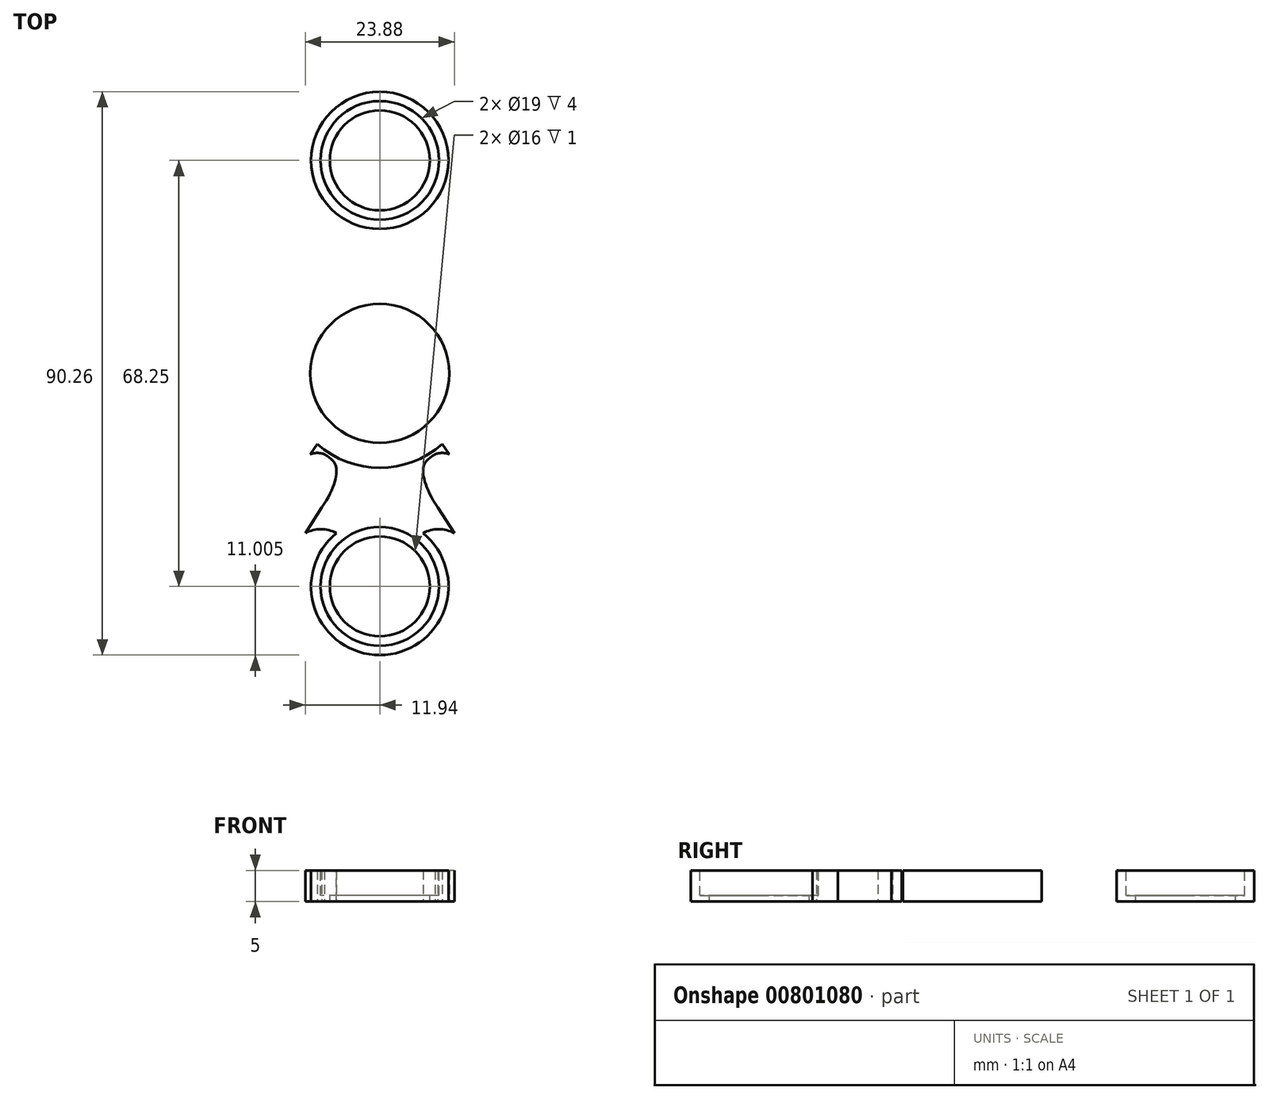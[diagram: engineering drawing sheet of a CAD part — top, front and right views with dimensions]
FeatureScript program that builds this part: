
annotation { "Feature Type Name" : "Feature", "Feature Type Description" : "" }
export const myFeature = defineFeature(function(context is Context, id is Id, definition is map)
    precondition{}
    {
        {
            var Q0;
            Q0=qCreatedBy(makeId("Top.planeOp"),FACE);
            var sketch = newSketch(context, id + "F0", { "sketchPlane" : qUnion([Q0])});
            skCircle(sketch, "E0", {"center": v(0, 0) * mm, "radius": 11.12 * mm});
            skCircle(sketch, "E1", {"center": v(0, 0) * mm, "radius": 15.12 * mm});
            skLineSegment(sketch, "E2", {"start": v(0, 15.12) * mm, "end": v(0, 45.12) * mm});
            skLineSegment(sketch, "E3", {"start": v(0, 45.12) * mm, "end": v(0, 23.12) * mm});
            skCircle(sketch, "E4", {"center": v(0, 34.12) * mm, "radius": 11 * mm});
            skLineSegment(sketch, "E5", {"start": v(0, 34.12) * mm, "end": v(-11, 34.12) * mm});
            skLineSegment(sketch, "E6", {"start": v(-10, 11.35) * mm, "end": v(-11.17, 12.98) * mm});
            skArc(sketch, "E7", {"start": v(-11.17, 12.98) * mm, "mid": v(-10, 12.75) * mm, "end": v(-8.84, 12.98) * mm});
            skArc(sketch, "E8", {"start": v(-11.94, 25.6) * mm, "mid": v(-9.45, 24.97) * mm, "end": v(-6.96, 25.6) * mm});
            skLineSegment(sketch, "E9", {"start": v(-11.94, 25.6) * mm, "end": v(-9.3, 21.5) * mm});
            skFitSpline(sketch, "E10", {"points": [v(-9.3, 21.5) * mm, v(-6.96, 15.22) * mm, v(-8.84, 12.98) * mm], "startDerivative": vector(9.24, -13.6) * mm, "endDerivative": vector(-10.35, -6.73) * mm});
            skLineSegment(sketch, "E11.MirrorCS", {"start": v(10, 11.35) * mm, "end": v(11.17, 12.98) * mm});
            skArc(sketch, "E12.MirrorCS", {"start": v(11.17, 12.98) * mm, "mid": v(10, 12.75) * mm, "end": v(8.84, 12.98) * mm});
            skFitSpline(sketch, "E13.MirrorCS", {"points": [v(9.3, 21.5) * mm, v(6.96, 15.22) * mm, v(8.84, 12.98) * mm], "startDerivative": vector(-9.24, -13.6) * mm, "endDerivative": vector(10.35, -6.73) * mm});
            skLineSegment(sketch, "E14.MirrorCS", {"start": v(11.94, 25.6) * mm, "end": v(9.3, 21.5) * mm});
            skArc(sketch, "E15.MirrorCS", {"start": v(11.94, 25.6) * mm, "mid": v(9.45, 24.97) * mm, "end": v(6.96, 25.6) * mm});
            skArc(sketch, "E16.MirrorCS", {"start": v(11.17, -12.98) * mm, "mid": v(10, -12.75) * mm, "end": v(8.84, -12.98) * mm});
            skLineSegment(sketch, "E17.MirrorCS", {"start": v(10, -11.35) * mm, "end": v(11.17, -12.98) * mm});
            skArc(sketch, "E18.MirrorCS", {"start": v(-11.17, -12.98) * mm, "mid": v(-10, -12.75) * mm, "end": v(-8.84, -12.98) * mm});
            skLineSegment(sketch, "E19.MirrorCS", {"start": v(-10, -11.35) * mm, "end": v(-11.17, -12.98) * mm});
            skArc(sketch, "E20.MirrorCS", {"start": v(11.94, -25.6) * mm, "mid": v(9.45, -24.97) * mm, "end": v(6.96, -25.6) * mm});
            skFitSpline(sketch, "E21.MirrorCS", {"points": [v(-9.3, -21.5) * mm, v(-6.96, -15.22) * mm, v(-8.84, -12.98) * mm], "startDerivative": vector(9.24, 13.6) * mm, "endDerivative": vector(-10.35, 6.73) * mm});
            skLineSegment(sketch, "E22.MirrorCS", {"start": v(-11.94, -25.6) * mm, "end": v(-9.3, -21.5) * mm});
            skArc(sketch, "E23.MirrorCS", {"start": v(-11.94, -25.6) * mm, "mid": v(-9.45, -24.97) * mm, "end": v(-6.96, -25.6) * mm});
            skLineSegment(sketch, "E24.MirrorCS", {"start": v(0, -34.12) * mm, "end": v(-11, -34.12) * mm});
            skCircle(sketch, "E25.MirrorC", {"center": v(0, -34.12) * mm, "radius": 11 * mm});
            skLineSegment(sketch, "E26.MirrorCS", {"start": v(0, -45.12) * mm, "end": v(0, -23.12) * mm});
            skLineSegment(sketch, "E27.MirrorCS", {"start": v(0, -15.12) * mm, "end": v(0, -45.12) * mm});
            skLineSegment(sketch, "E28.MirrorCS", {"start": v(11.94, -25.6) * mm, "end": v(9.3, -21.5) * mm});
            skFitSpline(sketch, "E29.MirrorCS", {"points": [v(9.3, -21.5) * mm, v(6.96, -15.22) * mm, v(8.84, -12.98) * mm], "startDerivative": vector(-9.24, 13.6) * mm, "endDerivative": vector(10.35, 6.73) * mm});
            skFitSpline(sketch, "E30.MirrorCS", {"points": [v(9.3, -21.5) * mm, v(6.96, -15.22) * mm, v(8.84, -12.98) * mm], "startDerivative": vector(-9.24, 13.6) * mm, "endDerivative": vector(10.35, 6.73) * mm});
            skLineSegment(sketch, "E31.MirrorCS", {"start": v(0, -34.12) * mm, "end": v(11, -34.12) * mm});
            skSolve(sketch);
        }
        {
            var Q0;
            Q0=makeQuery(id+"F0.imprint","IMPRINT",FACE,{"disambiguationData":[TD([[makeQuery(id+"F0.imprint","IMPRINT",EDGE,{"derivedFrom":sQuery(id+"F0.wireOp",EDGE,"E0")}),1.0]])]});
            var Q1;
            {var subQ0=sQuery(id+"F0.wireOp",EDGE,"E4");var subQ1=sQuery(id+"F0.wireOp",EDGE,"E3");var subQ2=makeQuery(id+"F0.imprint","INTERSECT",VERTEX,{"derivedFrom":[subQ1,subQ0]});Q1=makeQuery(id+"F0.imprint","IMPRINT",FACE,{"disambiguationData":[TD([[makeQuery(id+"F0.imprint","IMPRINT",EDGE,{"disambiguationData":[TD([[subQ2,-1.0]])],"derivedFrom":subQ1}),1.0]])]});}
            var Q2;
            {var subQ3=sQuery(id+"F0.wireOp",EDGE,"E5");Q2=makeQuery(id+"F0.imprint","IMPRINT",FACE,{"disambiguationData":[TD([[makeQuery(id+"F0.imprint","IMPRINT",EDGE,{"derivedFrom":subQ3}),1.0]])]});}
            var Q3;
            {var subQ3=sQuery(id+"F0.wireOp",EDGE,"E5");Q3=makeQuery(id+"F0.imprint","IMPRINT",FACE,{"disambiguationData":[TD([[makeQuery(id+"F0.imprint","IMPRINT",EDGE,{"derivedFrom":subQ3}),-1.0]])]});}
            var Q4;
            {var subQ2=sQuery(id+"F0.wireOp",EDGE,"E2");Q4=makeQuery(id+"F0.imprint","IMPRINT",FACE,{"disambiguationData":[TD([[makeQuery(id+"F0.imprint","IMPRINT",EDGE,{"derivedFrom":subQ2}),1.0]])]});}
            var Q5;
            {var subQ2=sQuery(id+"F0.wireOp",EDGE,"E2");Q5=makeQuery(id+"F0.imprint","IMPRINT",FACE,{"disambiguationData":[TD([[makeQuery(id+"F0.imprint","IMPRINT",EDGE,{"derivedFrom":subQ2}),-1.0]])]});}
            var Q6;
            {var subQ2=sQuery(id+"F0.wireOp",EDGE,"E17.MirrorCS");Q6=makeQuery(id+"F0.imprint","IMPRINT",FACE,{"disambiguationData":[TD([[makeQuery(id+"F0.imprint","IMPRINT",EDGE,{"derivedFrom":subQ2}),-1.0]])]});}
            var Q7;
            {var subQ6=sQuery(id+"F0.wireOp",EDGE,"E19.MirrorCS");Q7=makeQuery(id+"F0.imprint","IMPRINT",FACE,{"disambiguationData":[TD([[makeQuery(id+"F0.imprint","IMPRINT",EDGE,{"derivedFrom":subQ6}),1.0]])]});}
            var Q8;
            {var subQ0=sQuery(id+"F0.wireOp",EDGE,"E24.MirrorCS");Q8=makeQuery(id+"F0.imprint","IMPRINT",FACE,{"disambiguationData":[TD([[makeQuery(id+"F0.imprint","IMPRINT",EDGE,{"derivedFrom":subQ0}),-1.0]])]});}
            var Q9;
            {var subQ0=sQuery(id+"F0.wireOp",EDGE,"E31.MirrorCS");Q9=makeQuery(id+"F0.imprint","IMPRINT",FACE,{"disambiguationData":[TD([[makeQuery(id+"F0.imprint","IMPRINT",EDGE,{"derivedFrom":subQ0}),1.0]])]});}
            var Q10;
            {var subQ0=sQuery(id+"F0.wireOp",EDGE,"E31.MirrorCS");Q10=makeQuery(id+"F0.imprint","IMPRINT",FACE,{"disambiguationData":[TD([[makeQuery(id+"F0.imprint","IMPRINT",EDGE,{"derivedFrom":subQ0}),-1.0]])]});}
            var Q11;
            {var subQ0=sQuery(id+"F0.wireOp",EDGE,"E24.MirrorCS");Q11=makeQuery(id+"F0.imprint","IMPRINT",FACE,{"disambiguationData":[TD([[makeQuery(id+"F0.imprint","IMPRINT",EDGE,{"derivedFrom":subQ0}),1.0]])]});}
            extrude(context, id + "F1", {"entities" : qUnion([Q0, Q1, Q2, Q3, Q4, Q5, Q6, Q7, Q8, Q9, Q10, Q11]), "depth" : 5 * mm, "offsetDistance" : 25.4 * mm});
        }
        {
            var Q0;
            Q0=makeQuery(id+"F1.opExtrude","CAP_FACE",FACE,{"disambiguationData":[OSD([sQuery(id+"F0.wireOp",EDGE,"E4"),sQuery(id+"F0.wireOp",EDGE,"E6"),sQuery(id+"F0.wireOp",EDGE,"E7"),sQuery(id+"F0.wireOp",EDGE,"E8"),sQuery(id+"F0.wireOp",EDGE,"E9"),sQuery(id+"F0.wireOp",EDGE,"E10"),sQuery(id+"F0.wireOp",EDGE,"E11.MirrorCS"),sQuery(id+"F0.wireOp",EDGE,"E12.MirrorCS"),sQuery(id+"F0.wireOp",EDGE,"E13.MirrorCS"),sQuery(id+"F0.wireOp",EDGE,"E14.MirrorCS"),sQuery(id+"F0.wireOp",EDGE,"E15.MirrorCS"),sQuery(id+"F0.wireOp",EDGE,"E19.MirrorCS"),sQuery(id+"F0.wireOp",EDGE,"E18.MirrorCS"),sQuery(id+"F0.wireOp",EDGE,"E17.MirrorCS"),sQuery(id+"F0.wireOp",EDGE,"E16.MirrorCS"),sQuery(id+"F0.wireOp",EDGE,"E22.MirrorCS"),sQuery(id+"F0.wireOp",EDGE,"E23.MirrorCS"),sQuery(id+"F0.wireOp",EDGE,"E20.MirrorCS"),sQuery(id+"F0.wireOp",EDGE,"E1"),sQuery(id+"F0.wireOp",EDGE,"E28.MirrorCS"),sQuery(id+"F0.wireOp",EDGE,"E21.MirrorCS"),sQuery(id+"F0.wireOp",EDGE,"E30.MirrorCS"),sQuery(id+"F0.wireOp",EDGE,"E0"),sQuery(id+"F0.wireOp",EDGE,"E25.MirrorC")])],"isStart":false});
            var sketch = newSketch(context, id + "F2", { "sketchPlane" : qUnion([Q0])});
            skCircle(sketch, "E32", {"center": v(0, -34.12) * mm, "radius": 9.5 * mm});
            skCircle(sketch, "E33", {"center": v(0, 34.12) * mm, "radius": 9.5 * mm});
            skSolve(sketch);
        }
        {
            var Q0;
            Q0=makeQuery(id+"F2.imprint","IMPRINT",FACE,{"disambiguationData":[TD([[makeQuery(id+"F2.imprint","IMPRINT",EDGE,{"derivedFrom":sQuery(id+"F2.wireOp",EDGE,"E33")}),1.0]])]});
            var Q1;
            Q1=makeQuery(id+"F2.imprint","IMPRINT",FACE,{"disambiguationData":[TD([[makeQuery(id+"F2.imprint","IMPRINT",EDGE,{"derivedFrom":sQuery(id+"F2.wireOp",EDGE,"E32")}),1.0]])]});
            extrude(context, id + "F3", {"entities" : qUnion([Q0, Q1]), "operationType" : NewBodyOperationType.REMOVE, "oppositeDirection" : true, "depth" : 4 * mm, "offsetDistance" : 25.4 * mm});
        }
        {
            var Q0;
            Q0=makeQuery(id+"F3.boolean.opBoolean","COPY",FACE,{"derivedFrom":makeQuery(id+"F3.opExtrude","CAP_FACE",FACE,{"disambiguationData":[OSD([sQuery(id+"F2.wireOp",EDGE,"E32")])],"isStart":false})});
            var sketch = newSketch(context, id + "F4", { "sketchPlane" : qUnion([Q0])});
            skCircle(sketch, "E34", {"center": v(0, -34.12) * mm, "radius": 8 * mm});
            skSolve(sketch);
        }
        {
            var Q0;
            Q0=makeQuery(id+"F3.boolean.opBoolean","COPY",FACE,{"derivedFrom":makeQuery(id+"F3.opExtrude","CAP_FACE",FACE,{"disambiguationData":[OSD([sQuery(id+"F2.wireOp",EDGE,"E33")])],"isStart":false})});
            var sketch = newSketch(context, id + "F5", { "sketchPlane" : qUnion([Q0])});
            skCircle(sketch, "E35", {"center": v(0, 34.12) * mm, "radius": 8 * mm});
            skSolve(sketch);
        }
        {
            var Q0;
            Q0=makeQuery(id+"F5.imprint","IMPRINT",FACE,{"disambiguationData":[TD([[makeQuery(id+"F5.imprint","IMPRINT",EDGE,{"derivedFrom":sQuery(id+"F5.wireOp",EDGE,"E35")}),1.0]])]});
            var Q1;
            Q1=makeQuery(id+"F4.imprint","IMPRINT",FACE,{"disambiguationData":[TD([[makeQuery(id+"F4.imprint","IMPRINT",EDGE,{"derivedFrom":sQuery(id+"F4.wireOp",EDGE,"E34")}),1.0]])]});
            extrude(context, id + "F6", {"entities" : qUnion([Q0, Q1]), "operationType" : NewBodyOperationType.REMOVE, "endBound" : BoundingType.THROUGH_ALL, "oppositeDirection" : true, "depth" : 25.4 * mm, "offsetDistance" : 25.4 * mm});
        }
    });
